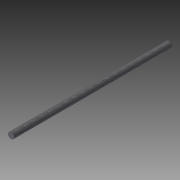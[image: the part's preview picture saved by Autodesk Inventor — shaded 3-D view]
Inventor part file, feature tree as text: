
AUTODESK INVENTOR PART (.ipt)
format: ipt  version: 2015 (Build 190159000, 159)  size: 69,120 bytes
history: native  units: mm
features: extrude x1, thread x1, sketch x1
ambient origin geometry x8: Origin, YZ Plane, XZ Plane, XY Plane, X Axis, Y Axis, Z Axis, Center Point
bodies: Solid1 (feature_tree)
feature tree (3):
  extrude  "Extrusion1"  Depth=205.0mm TaperAngle=0.0deg
  thread  "Thread1"  [1 undecoded]
  sketch  "Sketch1"  dims[d0=8.0mm d1=205.0mm d2=0.0mm d3=10.0mm d4=0.0mm]
note: 1 required parameter value undecoded (feature->parameter linkage not recoverable at this tier; creation-order binding heuristic only, values carry confidence <= 0.55)
